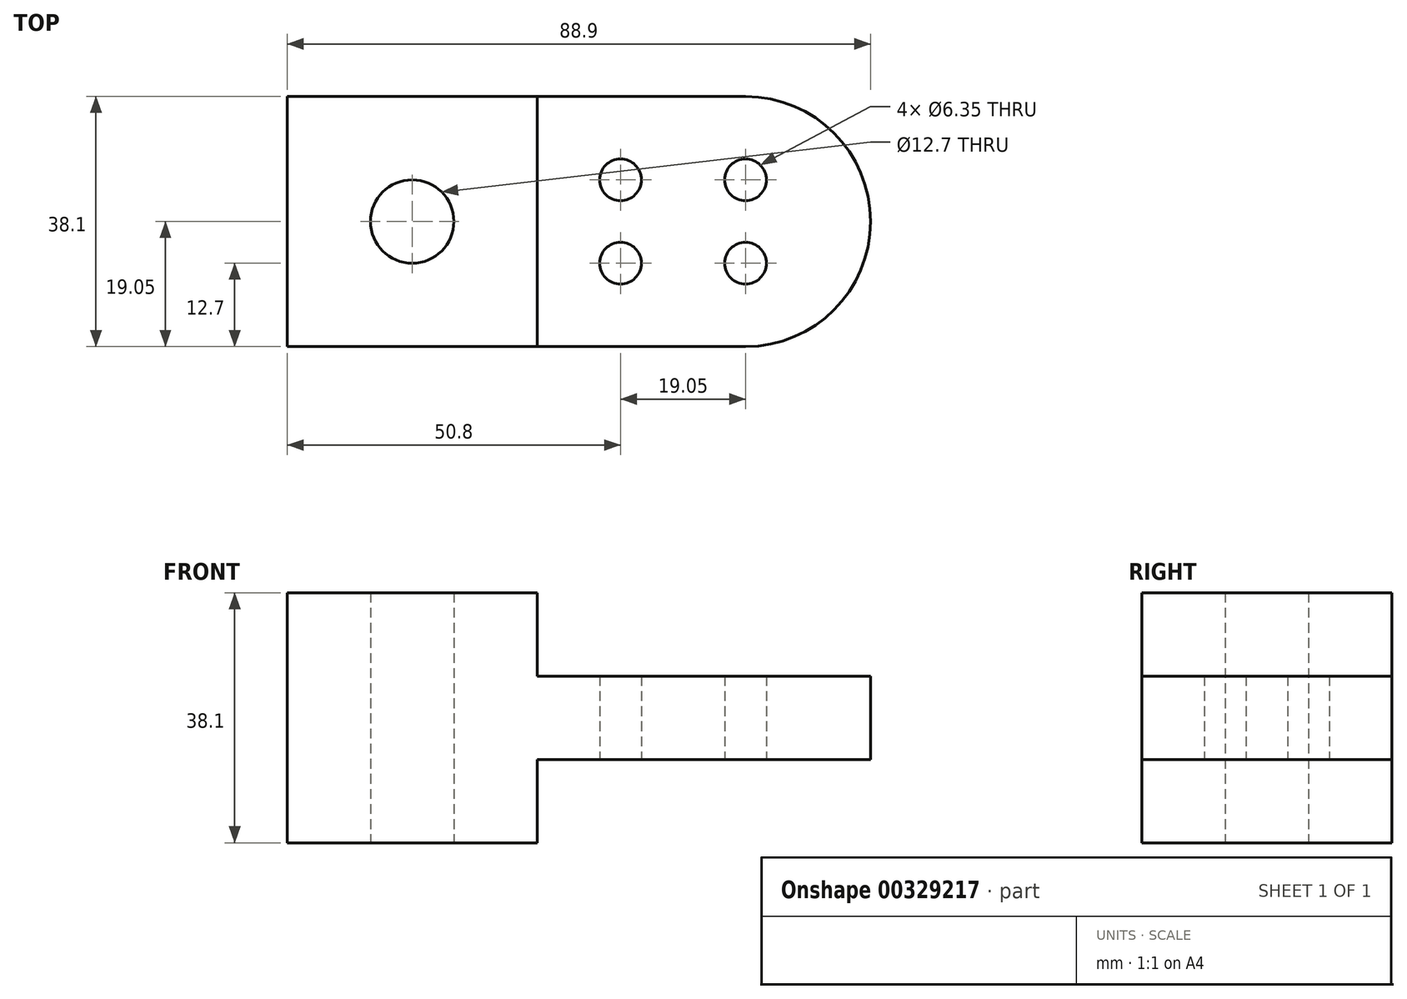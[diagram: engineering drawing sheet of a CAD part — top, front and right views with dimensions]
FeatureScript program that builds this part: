
annotation { "Feature Type Name" : "Feature", "Feature Type Description" : "" }
export const myFeature = defineFeature(function(context is Context, id is Id, definition is map)
    precondition{}
    {
        {
            var Q0;
            Q0=qCreatedBy(makeId("Front.planeOp"),FACE);
            var sketch = newSketch(context, id + "F0", { "sketchPlane" : qUnion([Q0])});
            skLineSegment(sketch, "E0.bottom", {"start": v(0, 0) * mm, "end": v(38.1, 0) * mm});
            skLineSegment(sketch, "E0.top", {"start": v(0, 38.1) * mm, "end": v(38.1, 38.1) * mm});
            skLineSegment(sketch, "E0.left", {"start": v(0, 0) * mm, "end": v(0, 38.1) * mm});
            skLineSegment(sketch, "E0.right", {"start": v(38.1, 0) * mm, "end": v(38.1, 12.7) * mm});
            skLineSegment(sketch, "E1.bottom", {"start": v(38.1, 25.4) * mm, "end": v(88.9, 25.4) * mm});
            skLineSegment(sketch, "E1.top", {"start": v(38.1, 12.7) * mm, "end": v(88.9, 12.7) * mm});
            skLineSegment(sketch, "E1.right", {"start": v(88.9, 25.4) * mm, "end": v(88.9, 12.7) * mm});
            skLineSegment(sketch, "E2.trimOffspring", {"start": v(38.1, 25.4) * mm, "end": v(38.1, 38.1) * mm});
            skSolve(sketch);
        }
        {
            var Q0;
            Q0=qCreatedBy(makeId("Top.planeOp"),FACE);
            var sketch = newSketch(context, id + "F1", { "sketchPlane" : qUnion([Q0])});
            skLineSegment(sketch, "E3.bottom", {"start": v(0, 0) * mm, "end": v(38.1, 0) * mm});
            skLineSegment(sketch, "E3.top", {"start": v(0, 38.1) * mm, "end": v(38.1, 38.1) * mm});
            skLineSegment(sketch, "E3.left", {"start": v(0, 0) * mm, "end": v(0, 38.1) * mm});
            skLineSegment(sketch, "E3.right", {"start": v(38.1, 0) * mm, "end": v(38.1, 38.1) * mm});
            skLineSegment(sketch, "E4.bottom", {"start": v(38.1, 38.1) * mm, "end": v(69.85, 38.1) * mm});
            skLineSegment(sketch, "E4.top", {"start": v(38.1, 0) * mm, "end": v(69.85, 0) * mm});
            skLineSegment(sketch, "E4.left", {"start": v(38.1, 38.1) * mm, "end": v(38.1, 0) * mm});
            skArc(sketch, "E5", {"start": v(69.85, 0) * mm, "mid": v(88.9, 19.05) * mm, "end": v(69.85, 38.1) * mm});
            skCircle(sketch, "E6", {"center": v(19.05, 19.05) * mm, "radius": 6.35 * mm});
            skCircle(sketch, "E7", {"center": v(50.8, 25.4) * mm, "radius": 3.18 * mm});
            skCircle(sketch, "E8", {"center": v(69.85, 25.4) * mm, "radius": 3.18 * mm});
            skCircle(sketch, "E9", {"center": v(50.8, 12.7) * mm, "radius": 3.18 * mm});
            skCircle(sketch, "E10", {"center": v(69.85, 12.7) * mm, "radius": 3.18 * mm});
            skSolve(sketch);
        }
        {
            var Q0;
            Q0 = qSketchRegion(id + "F1", true);
            extrude(context, id + "F2", {"entities" : qUnion([Q0]), "depth" : 25.4 * mm});
        }
        {
            var Q0;
            Q0=qCreatedBy(makeId("Front.planeOp"),FACE);
            var sketch = newSketch(context, id + "F3", { "sketchPlane" : qUnion([Q0])});
            skLineSegment(sketch, "E11", {"start": v(38.1, 0) * mm, "end": v(38.1, 12.7) * mm});
            skLineSegment(sketch, "E12", {"start": v(38.1, 12.7) * mm, "end": v(88.9, 12.7) * mm});
            skLineSegment(sketch, "E13", {"start": v(88.9, 12.7) * mm, "end": v(88.9, 0) * mm});
            skLineSegment(sketch, "E14", {"start": v(88.9, 0) * mm, "end": v(38.1, 0) * mm});
            skSolve(sketch);
        }
        {
            var Q0;
            Q0 = qSketchRegion(id + "F3", true);
            extrude(context, id + "F4", {"entities" : qUnion([Q0]), "operationType" : NewBodyOperationType.REMOVE, "endBound" : BoundingType.THROUGH_ALL, "oppositeDirection" : true, "depth" : 25.4 * mm});
        }
        {
            var Q0;
            Q0=qCreatedBy(makeId("Front.planeOp"),FACE);
            var sketch = newSketch(context, id + "F5", { "sketchPlane" : qUnion([Q0])});
            skLineSegment(sketch, "E15", {"start": v(0, 25.4) * mm, "end": v(0, 38.1) * mm});
            skLineSegment(sketch, "E16", {"start": v(0, 38.1) * mm, "end": v(38.1, 38.1) * mm});
            skLineSegment(sketch, "E17", {"start": v(0, 25.4) * mm, "end": v(38.1, 25.4) * mm});
            skLineSegment(sketch, "E18", {"start": v(38.1, 25.4) * mm, "end": v(38.1, 38.1) * mm});
            skSolve(sketch);
        }
        {
            var Q0;
            Q0 = qSketchRegion(id + "F5", true);
            extrude(context, id + "F6", {"entities" : qUnion([Q0]), "operationType" : NewBodyOperationType.ADD, "oppositeDirection" : true, "depth" : 38.1 * mm});
        }
        {
            var Q0;
            Q0=makeQuery(id+"F6.opExtrude","SWEPT_FACE",FACE,{"disambiguationData":[OSD([sQuery(id+"F5.wireOp",EDGE,"E16")])]});
            var sketch = newSketch(context, id + "F7", { "sketchPlane" : qUnion([Q0])});
            skCircle(sketch, "E19", {"center": v(19.05, 19.05) * mm, "radius": 6.35 * mm});
            skSolve(sketch);
        }
        {
            var Q0;
            Q0 = qSketchRegion(id + "F7", true);
            extrude(context, id + "F8", {"entities" : qUnion([Q0]), "operationType" : NewBodyOperationType.REMOVE, "endBound" : BoundingType.THROUGH_ALL, "oppositeDirection" : true, "depth" : 25.4 * mm});
        }
    });
